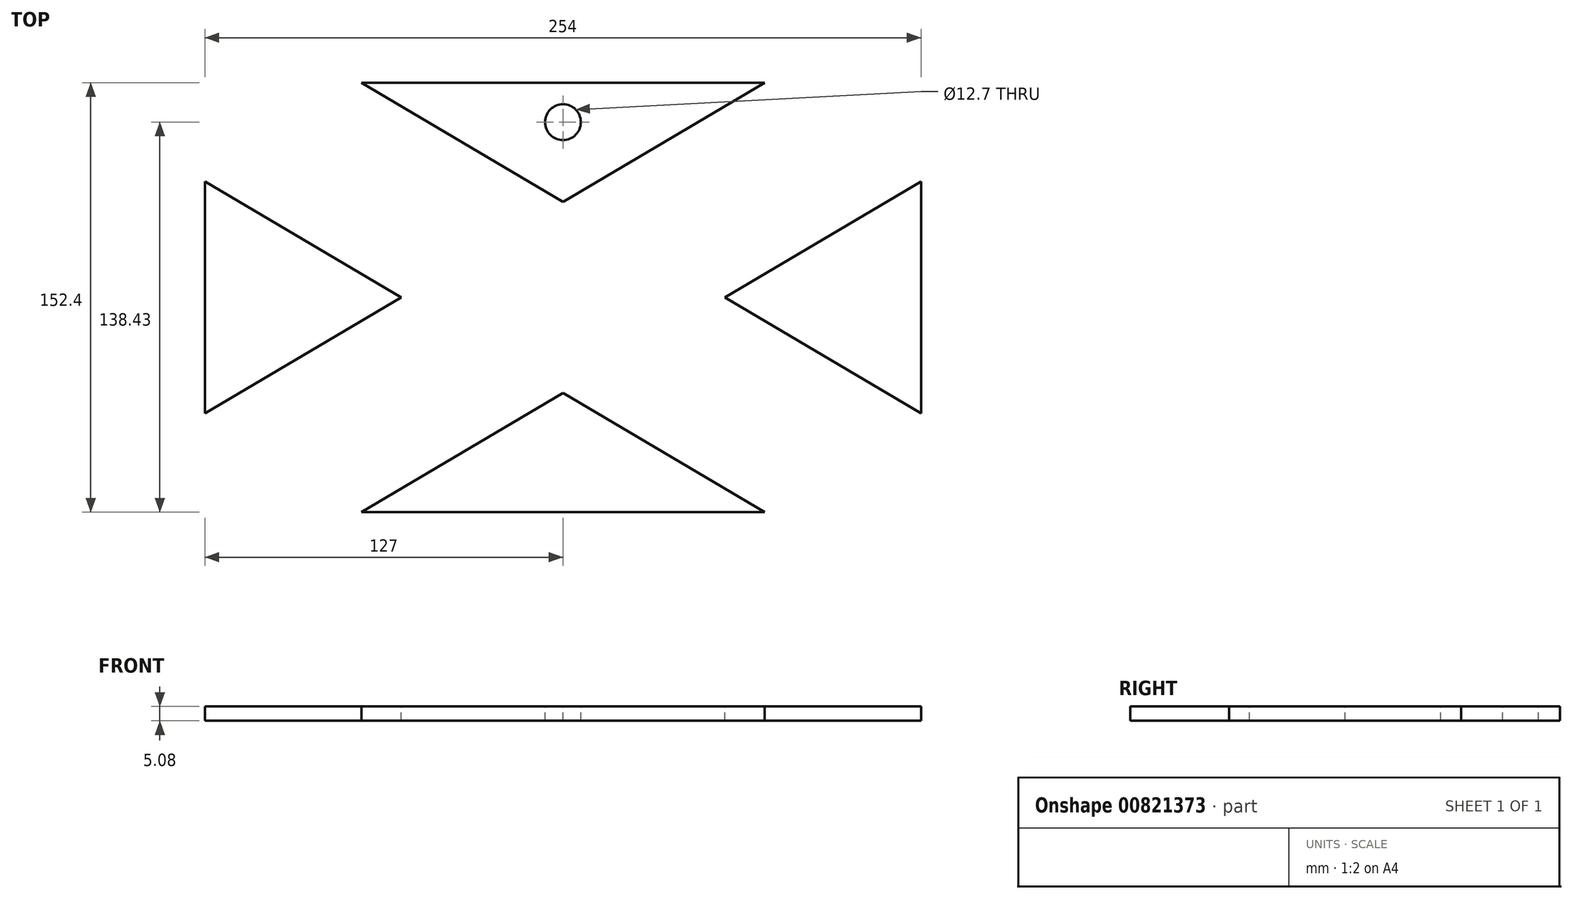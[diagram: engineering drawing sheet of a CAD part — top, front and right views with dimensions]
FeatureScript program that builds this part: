
annotation { "Feature Type Name" : "Feature", "Feature Type Description" : "" }
export const myFeature = defineFeature(function(context is Context, id is Id, definition is map)
    precondition{}
    {
        {
            var Q0;
            Q0=qCreatedBy(makeId("Top.planeOp"),FACE);
            var sketch = newSketch(context, id + "F0", { "sketchPlane" : qUnion([Q0])});
            skLineSegment(sketch, "E0.bottom", {"start": v(127, -76.2) * mm, "end": v(-127, -76.2) * mm});
            skLineSegment(sketch, "E0.top", {"start": v(127, 76.2) * mm, "end": v(-127, 76.2) * mm});
            skLineSegment(sketch, "E0.left", {"start": v(127, -76.2) * mm, "end": v(127, 76.2) * mm});
            skLineSegment(sketch, "E0.right", {"start": v(-127, -76.2) * mm, "end": v(-127, 76.2) * mm});
            skPoint(sketch, "E0.middle", {"position": v(0, 0) * mm});
            skSolve(sketch);
        }
        {
            var Q0;
            Q0=makeQuery(id+"F0.imprint","IMPRINT",FACE,{"disambiguationData":[TD([[makeQuery(id+"F0.imprint","IMPRINT",EDGE,{"derivedFrom":sQuery(id+"F0.wireOp",EDGE,"E0.bottom")}),-1.0]])]});
            var sketch = newSketch(context, id + "F1", { "sketchPlane" : qUnion([Q0])});
            skLineSegment(sketch, "E1.0", {"start": v(-127, -76.2) * mm, "end": v(-127, -55.88) * mm});
            skLineSegment(sketch, "E2.0", {"start": v(127, -76.2) * mm, "end": v(127, -55.88) * mm});
            skLineSegment(sketch, "E3.0", {"start": v(127, 76.2) * mm, "end": v(96.48, 76.2) * mm});
            skLineSegment(sketch, "E4.0", {"start": v(127, -76.2) * mm, "end": v(96.48, -76.2) * mm});
            skLineSegment(sketch, "E5", {"start": v(-127, -55.88) * mm, "end": v(96.48, 76.2) * mm});
            skLineSegment(sketch, "E6", {"start": v(-96.48, -76.2) * mm, "end": v(127, 55.88) * mm});
            skLineSegment(sketch, "E7", {"start": v(-127, 55.88) * mm, "end": v(96.48, -76.2) * mm});
            skLineSegment(sketch, "E8", {"start": v(127, -55.88) * mm, "end": v(-96.48, 76.2) * mm});
            skLineSegment(sketch, "E9.trimOffspring", {"start": v(-127, 55.88) * mm, "end": v(-127, 76.2) * mm});
            skLineSegment(sketch, "E10.trimOffspring", {"start": v(-96.48, 76.2) * mm, "end": v(-127, 76.2) * mm});
            skLineSegment(sketch, "E11.trimOffspring", {"start": v(127, 55.88) * mm, "end": v(127, 76.2) * mm});
            skLineSegment(sketch, "E12.trimOffspring", {"start": v(-96.48, -76.2) * mm, "end": v(-127, -76.2) * mm});
            skSolve(sketch);
        }
        {
            var Q0;
            Q0=makeQuery(id+"F0.imprint","IMPRINT",FACE,{"disambiguationData":[TD([[makeQuery(id+"F0.imprint","IMPRINT",EDGE,{"derivedFrom":sQuery(id+"F0.wireOp",EDGE,"E0.bottom")}),-1.0]])]});
            extrude(context, id + "F2", {"entities" : qUnion([Q0]), "depth" : 5.08 * mm, "offsetDistance" : 25.4 * mm});
        }
        {
            var Q0;
            Q0 = qSketchRegion(id + "F1", true);
            extrude(context, id + "F3", {"entities" : qUnion([Q0]), "depth" : 4.57 * mm, "offsetDistance" : 25.4 * mm});
        }
        {
            var Q0;
            Q0=makeQuery(id+"F3.opExtrude","CAP_FACE",FACE,{"disambiguationData":[OSD([sQuery(id+"F1.wireOp",EDGE,"E1.0"),sQuery(id+"F1.wireOp",EDGE,"E2.0"),sQuery(id+"F1.wireOp",EDGE,"E3.0"),sQuery(id+"F1.wireOp",EDGE,"E4.0"),sQuery(id+"F1.wireOp",EDGE,"E5"),sQuery(id+"F1.wireOp",EDGE,"E6"),sQuery(id+"F1.wireOp",EDGE,"E7"),sQuery(id+"F1.wireOp",EDGE,"E8"),sQuery(id+"F1.wireOp",EDGE,"E9.trimOffspring"),sQuery(id+"F1.wireOp",EDGE,"E10.trimOffspring"),sQuery(id+"F1.wireOp",EDGE,"E11.trimOffspring"),sQuery(id+"F1.wireOp",EDGE,"E12.trimOffspring")])],"isStart":false});
            var sketch = newSketch(context, id + "F4", { "sketchPlane" : qUnion([Q0])});
            skLineSegment(sketch, "E13", {"start": v(-47.84, 13) * mm, "end": v(-39.34, 19.17) * mm});
            skLineSegment(sketch, "E14", {"start": v(-25.6, 29.15) * mm, "end": v(-36.1, 29.15) * mm});
            skLineSegment(sketch, "E15", {"start": v(-53.09, 29.15) * mm, "end": v(-44.6, 22.98) * mm});
            skLineSegment(sketch, "E16", {"start": v(-30.85, 13) * mm, "end": v(-34.1, 22.98) * mm});
            skLineSegment(sketch, "E17", {"start": v(-39.34, 39.14) * mm, "end": v(-42.59, 29.15) * mm});
            skLineSegment(sketch, "E18", {"start": v(-79.1, 30.34) * mm, "end": v(-70.6, 36.5) * mm});
            skLineSegment(sketch, "E19", {"start": v(-56.85, 46.5) * mm, "end": v(-67.35, 46.5) * mm});
            skLineSegment(sketch, "E20", {"start": v(-84.34, 46.5) * mm, "end": v(-75.85, 40.32) * mm});
            skLineSegment(sketch, "E21", {"start": v(-62.1, 30.34) * mm, "end": v(-65.35, 40.32) * mm});
            skLineSegment(sketch, "E22", {"start": v(-70.6, 56.48) * mm, "end": v(-73.84, 46.5) * mm});
            skLineSegment(sketch, "E23", {"start": v(-110.4, 48.48) * mm, "end": v(-101.9, 54.65) * mm});
            skLineSegment(sketch, "E24", {"start": v(-88.16, 64.64) * mm, "end": v(-98.66, 64.64) * mm});
            skLineSegment(sketch, "E25", {"start": v(-115.65, 64.64) * mm, "end": v(-107.16, 58.46) * mm});
            skLineSegment(sketch, "E26", {"start": v(-93.41, 48.48) * mm, "end": v(-96.66, 58.46) * mm});
            skLineSegment(sketch, "E27", {"start": v(-101.9, 74.62) * mm, "end": v(-105.15, 64.64) * mm});
            skLineSegment(sketch, "E28.trimOffspring", {"start": v(-98.66, 64.64) * mm, "end": v(-101.9, 74.62) * mm});
            skLineSegment(sketch, "E29.trimOffspring", {"start": v(-105.15, 64.64) * mm, "end": v(-115.65, 64.64) * mm});
            skLineSegment(sketch, "E30.trimOffspring", {"start": v(-107.16, 58.46) * mm, "end": v(-110.4, 48.48) * mm});
            skLineSegment(sketch, "E31.trimOffspring", {"start": v(-101.9, 54.65) * mm, "end": v(-93.41, 48.48) * mm});
            skLineSegment(sketch, "E32.trimOffspring", {"start": v(-96.66, 58.46) * mm, "end": v(-88.16, 64.64) * mm});
            skLineSegment(sketch, "E33.trimOffspring", {"start": v(-75.85, 40.32) * mm, "end": v(-79.1, 30.34) * mm});
            skLineSegment(sketch, "E34.trimOffspring", {"start": v(-73.84, 46.5) * mm, "end": v(-84.34, 46.5) * mm});
            skLineSegment(sketch, "E35.trimOffspring", {"start": v(-67.35, 46.5) * mm, "end": v(-70.6, 56.48) * mm});
            skLineSegment(sketch, "E36.trimOffspring", {"start": v(-65.35, 40.32) * mm, "end": v(-56.85, 46.5) * mm});
            skLineSegment(sketch, "E37.trimOffspring", {"start": v(-70.6, 36.5) * mm, "end": v(-62.1, 30.34) * mm});
            skLineSegment(sketch, "E38.trimOffspring", {"start": v(-44.6, 22.98) * mm, "end": v(-47.84, 13) * mm});
            skLineSegment(sketch, "E39.trimOffspring", {"start": v(-42.59, 29.15) * mm, "end": v(-53.09, 29.15) * mm});
            skLineSegment(sketch, "E40.trimOffspring", {"start": v(-36.1, 29.15) * mm, "end": v(-39.34, 39.14) * mm});
            skLineSegment(sketch, "E41.trimOffspring", {"start": v(-34.1, 22.98) * mm, "end": v(-25.6, 29.15) * mm});
            skLineSegment(sketch, "E42.trimOffspring", {"start": v(-39.34, 19.17) * mm, "end": v(-30.85, 13) * mm});
            skLineSegment(sketch, "E43", {"start": v(92.71, 48.72) * mm, "end": v(101.2, 54.9) * mm});
            skLineSegment(sketch, "E44", {"start": v(114.95, 64.88) * mm, "end": v(104.45, 64.88) * mm});
            skLineSegment(sketch, "E45", {"start": v(87.46, 64.88) * mm, "end": v(95.96, 58.7) * mm});
            skLineSegment(sketch, "E46", {"start": v(109.7, 48.72) * mm, "end": v(106.46, 58.7) * mm});
            skLineSegment(sketch, "E47", {"start": v(101.2, 74.86) * mm, "end": v(97.96, 64.88) * mm});
            skLineSegment(sketch, "E48", {"start": v(60.3, 28.22) * mm, "end": v(68.8, 34.4) * mm});
            skLineSegment(sketch, "E49", {"start": v(82.54, 44.38) * mm, "end": v(72.04, 44.38) * mm});
            skLineSegment(sketch, "E50", {"start": v(55.05, 44.38) * mm, "end": v(63.54, 38.2) * mm});
            skLineSegment(sketch, "E51", {"start": v(77.29, 28.22) * mm, "end": v(74.04, 38.2) * mm});
            skLineSegment(sketch, "E52", {"start": v(68.8, 54.36) * mm, "end": v(65.55, 44.38) * mm});
            skLineSegment(sketch, "E53", {"start": v(26.46, 9.39) * mm, "end": v(34.95, 15.56) * mm});
            skLineSegment(sketch, "E54", {"start": v(48.7, 25.54) * mm, "end": v(38.2, 25.54) * mm});
            skLineSegment(sketch, "E55", {"start": v(21.2, 25.54) * mm, "end": v(29.7, 19.37) * mm});
            skLineSegment(sketch, "E56", {"start": v(43.45, 9.39) * mm, "end": v(40.2, 19.37) * mm});
            skLineSegment(sketch, "E57", {"start": v(34.95, 35.53) * mm, "end": v(31.7, 25.54) * mm});
            skLineSegment(sketch, "E58.trimOffspring", {"start": v(31.7, 25.54) * mm, "end": v(21.2, 25.54) * mm});
            skLineSegment(sketch, "E59.trimOffspring", {"start": v(29.7, 19.37) * mm, "end": v(26.46, 9.39) * mm});
            skLineSegment(sketch, "E60.trimOffspring", {"start": v(34.95, 15.56) * mm, "end": v(43.45, 9.39) * mm});
            skLineSegment(sketch, "E61.trimOffspring", {"start": v(40.2, 19.37) * mm, "end": v(48.7, 25.54) * mm});
            skLineSegment(sketch, "E62.trimOffspring", {"start": v(38.2, 25.54) * mm, "end": v(34.95, 35.53) * mm});
            skLineSegment(sketch, "E63.trimOffspring", {"start": v(63.54, 38.2) * mm, "end": v(60.3, 28.22) * mm});
            skLineSegment(sketch, "E64.trimOffspring", {"start": v(68.8, 34.4) * mm, "end": v(77.29, 28.22) * mm});
            skLineSegment(sketch, "E65.trimOffspring", {"start": v(74.04, 38.2) * mm, "end": v(82.54, 44.38) * mm});
            skLineSegment(sketch, "E66.trimOffspring", {"start": v(72.04, 44.38) * mm, "end": v(68.8, 54.36) * mm});
            skLineSegment(sketch, "E67.trimOffspring", {"start": v(65.55, 44.38) * mm, "end": v(55.05, 44.38) * mm});
            skLineSegment(sketch, "E68.trimOffspring", {"start": v(95.96, 58.7) * mm, "end": v(92.71, 48.72) * mm});
            skLineSegment(sketch, "E69.trimOffspring", {"start": v(106.46, 58.7) * mm, "end": v(114.95, 64.88) * mm});
            skLineSegment(sketch, "E70.trimOffspring", {"start": v(101.2, 54.9) * mm, "end": v(109.7, 48.72) * mm});
            skLineSegment(sketch, "E71.trimOffspring", {"start": v(97.96, 64.88) * mm, "end": v(87.46, 64.88) * mm});
            skLineSegment(sketch, "E72.trimOffspring", {"start": v(104.45, 64.88) * mm, "end": v(101.2, 74.86) * mm});
            skLineSegment(sketch, "E73", {"start": v(98.34, -73.56) * mm, "end": v(106.84, -67.39) * mm});
            skLineSegment(sketch, "E74", {"start": v(120.58, -57.4) * mm, "end": v(110.08, -57.4) * mm});
            skLineSegment(sketch, "E75", {"start": v(93.1, -57.4) * mm, "end": v(101.59, -63.57) * mm});
            skLineSegment(sketch, "E76", {"start": v(115.33, -73.56) * mm, "end": v(112.09, -63.57) * mm});
            skLineSegment(sketch, "E77", {"start": v(106.84, -47.41) * mm, "end": v(103.6, -57.4) * mm});
            skLineSegment(sketch, "E78", {"start": v(66.16, -55.85) * mm, "end": v(74.65, -49.67) * mm});
            skLineSegment(sketch, "E79", {"start": v(88.4, -39.69) * mm, "end": v(77.9, -39.69) * mm});
            skLineSegment(sketch, "E80", {"start": v(60.9, -39.69) * mm, "end": v(69.4, -45.86) * mm});
            skLineSegment(sketch, "E81", {"start": v(83.15, -55.85) * mm, "end": v(79.9, -45.86) * mm});
            skLineSegment(sketch, "E82", {"start": v(74.65, -29.7) * mm, "end": v(71.4, -39.69) * mm});
            skLineSegment(sketch, "E83", {"start": v(33.1, -36.4) * mm, "end": v(41.6, -30.23) * mm});
            skLineSegment(sketch, "E84", {"start": v(55.35, -20.25) * mm, "end": v(44.85, -20.25) * mm});
            skLineSegment(sketch, "E85", {"start": v(27.86, -20.25) * mm, "end": v(36.35, -26.42) * mm});
            skLineSegment(sketch, "E86", {"start": v(50.1, -36.4) * mm, "end": v(46.85, -26.42) * mm});
            skLineSegment(sketch, "E87", {"start": v(41.6, -10.26) * mm, "end": v(38.36, -20.25) * mm});
            skLineSegment(sketch, "E88.trimOffspring", {"start": v(44.85, -20.25) * mm, "end": v(41.6, -10.26) * mm});
            skLineSegment(sketch, "E89.trimOffspring", {"start": v(38.36, -20.25) * mm, "end": v(27.86, -20.25) * mm});
            skLineSegment(sketch, "E90.trimOffspring", {"start": v(36.35, -26.42) * mm, "end": v(33.1, -36.4) * mm});
            skLineSegment(sketch, "E91.trimOffspring", {"start": v(41.6, -30.23) * mm, "end": v(50.1, -36.4) * mm});
            skLineSegment(sketch, "E92.trimOffspring", {"start": v(46.85, -26.42) * mm, "end": v(55.35, -20.25) * mm});
            skLineSegment(sketch, "E93.trimOffspring", {"start": v(71.4, -39.69) * mm, "end": v(60.9, -39.69) * mm});
            skLineSegment(sketch, "E94.trimOffspring", {"start": v(69.4, -45.86) * mm, "end": v(66.16, -55.85) * mm});
            skLineSegment(sketch, "E95.trimOffspring", {"start": v(74.65, -49.67) * mm, "end": v(83.15, -55.85) * mm});
            skLineSegment(sketch, "E96.trimOffspring", {"start": v(79.9, -45.86) * mm, "end": v(88.4, -39.69) * mm});
            skLineSegment(sketch, "E97.trimOffspring", {"start": v(77.9, -39.69) * mm, "end": v(74.65, -29.7) * mm});
            skLineSegment(sketch, "E98.trimOffspring", {"start": v(103.6, -57.4) * mm, "end": v(93.1, -57.4) * mm});
            skLineSegment(sketch, "E99.trimOffspring", {"start": v(101.59, -63.57) * mm, "end": v(98.34, -73.56) * mm});
            skLineSegment(sketch, "E100.trimOffspring", {"start": v(106.84, -67.39) * mm, "end": v(115.33, -73.56) * mm});
            skLineSegment(sketch, "E101.trimOffspring", {"start": v(112.09, -63.57) * mm, "end": v(120.58, -57.4) * mm});
            skLineSegment(sketch, "E102.trimOffspring", {"start": v(110.08, -57.4) * mm, "end": v(106.84, -47.41) * mm});
            skLineSegment(sketch, "E103", {"start": v(-113.93, -72.57) * mm, "end": v(-105.44, -66.4) * mm});
            skLineSegment(sketch, "E104", {"start": v(-91.7, -56.41) * mm, "end": v(-102.2, -56.41) * mm});
            skLineSegment(sketch, "E105", {"start": v(-119.18, -56.41) * mm, "end": v(-110.69, -62.58) * mm});
            skLineSegment(sketch, "E106", {"start": v(-96.94, -72.57) * mm, "end": v(-100.19, -62.58) * mm});
            skLineSegment(sketch, "E107", {"start": v(-105.44, -46.43) * mm, "end": v(-108.68, -56.41) * mm});
            skLineSegment(sketch, "E108", {"start": v(-80.55, -53.31) * mm, "end": v(-72.06, -47.14) * mm});
            skLineSegment(sketch, "E109", {"start": v(-58.31, -37.15) * mm, "end": v(-68.81, -37.15) * mm});
            skLineSegment(sketch, "E110", {"start": v(-85.8, -37.15) * mm, "end": v(-77.3, -43.33) * mm});
            skLineSegment(sketch, "E111", {"start": v(-63.56, -53.31) * mm, "end": v(-66.8, -43.33) * mm});
            skLineSegment(sketch, "E112", {"start": v(-72.06, -27.17) * mm, "end": v(-75.3, -37.15) * mm});
            skLineSegment(sketch, "E113", {"start": v(-45.52, -32.65) * mm, "end": v(-37.02, -26.48) * mm});
            skLineSegment(sketch, "E114", {"start": v(-23.28, -16.5) * mm, "end": v(-33.78, -16.5) * mm});
            skLineSegment(sketch, "E115", {"start": v(-50.77, -16.5) * mm, "end": v(-42.27, -22.66) * mm});
            skLineSegment(sketch, "E116", {"start": v(-28.53, -32.65) * mm, "end": v(-31.77, -22.66) * mm});
            skLineSegment(sketch, "E117", {"start": v(-37.02, -6.5) * mm, "end": v(-40.27, -16.5) * mm});
            skLineSegment(sketch, "E118.trimOffspring", {"start": v(-40.27, -16.5) * mm, "end": v(-50.77, -16.5) * mm});
            skLineSegment(sketch, "E119.trimOffspring", {"start": v(-42.27, -22.66) * mm, "end": v(-45.52, -32.65) * mm});
            skLineSegment(sketch, "E120.trimOffspring", {"start": v(-37.02, -26.48) * mm, "end": v(-28.53, -32.65) * mm});
            skLineSegment(sketch, "E121.trimOffspring", {"start": v(-31.77, -22.66) * mm, "end": v(-23.28, -16.5) * mm});
            skLineSegment(sketch, "E122.trimOffspring", {"start": v(-33.78, -16.5) * mm, "end": v(-37.02, -6.5) * mm});
            skLineSegment(sketch, "E123.trimOffspring", {"start": v(-75.3, -37.15) * mm, "end": v(-85.8, -37.15) * mm});
            skLineSegment(sketch, "E124.trimOffspring", {"start": v(-77.3, -43.33) * mm, "end": v(-80.55, -53.31) * mm});
            skLineSegment(sketch, "E125.trimOffspring", {"start": v(-72.06, -47.14) * mm, "end": v(-63.56, -53.31) * mm});
            skLineSegment(sketch, "E126.trimOffspring", {"start": v(-66.8, -43.33) * mm, "end": v(-58.31, -37.15) * mm});
            skLineSegment(sketch, "E127.trimOffspring", {"start": v(-68.81, -37.15) * mm, "end": v(-72.06, -27.17) * mm});
            skLineSegment(sketch, "E128.trimOffspring", {"start": v(-108.68, -56.41) * mm, "end": v(-119.18, -56.41) * mm});
            skLineSegment(sketch, "E129.trimOffspring", {"start": v(-110.69, -62.58) * mm, "end": v(-113.93, -72.57) * mm});
            skLineSegment(sketch, "E130.trimOffspring", {"start": v(-105.44, -66.4) * mm, "end": v(-96.94, -72.57) * mm});
            skLineSegment(sketch, "E131.trimOffspring", {"start": v(-100.19, -62.58) * mm, "end": v(-91.7, -56.41) * mm});
            skLineSegment(sketch, "E132.trimOffspring", {"start": v(-102.2, -56.41) * mm, "end": v(-105.44, -46.43) * mm});
            skLineSegment(sketch, "E133", {"start": v(-8.5, -11.7) * mm, "end": v(0, -5.52) * mm});
            skLineSegment(sketch, "E134", {"start": v(13.74, 4.47) * mm, "end": v(3.24, 4.47) * mm});
            skLineSegment(sketch, "E135", {"start": v(-13.74, 4.47) * mm, "end": v(-5.25, -1.7) * mm});
            skLineSegment(sketch, "E136", {"start": v(8.5, -11.7) * mm, "end": v(5.25, -1.7) * mm});
            skLineSegment(sketch, "E137", {"start": v(0, 14.45) * mm, "end": v(-3.24, 4.47) * mm});
            skLineSegment(sketch, "E138.trimOffspring", {"start": v(3.24, 4.47) * mm, "end": v(0, 14.45) * mm});
            skLineSegment(sketch, "E139.trimOffspring", {"start": v(-3.24, 4.47) * mm, "end": v(-13.74, 4.47) * mm});
            skLineSegment(sketch, "E140.trimOffspring", {"start": v(-5.25, -1.7) * mm, "end": v(-8.5, -11.7) * mm});
            skLineSegment(sketch, "E141.trimOffspring", {"start": v(0, -5.52) * mm, "end": v(8.5, -11.7) * mm});
            skLineSegment(sketch, "E142.trimOffspring", {"start": v(5.25, -1.7) * mm, "end": v(13.74, 4.47) * mm});
            skSolve(sketch);
        }
        {
            var Q0;
            Q0 = qSketchRegion(id + "F4", true);
            extrude(context, id + "F5", {"entities" : qUnion([Q0]), "depth" : 0.5 * mm, "offsetDistance" : 25.4 * mm});
        }
        {
            var Q0;
            Q0=makeQuery(id+"F2.opExtrude","CAP_FACE",FACE,{"disambiguationData":[OSD([sQuery(id+"F0.wireOp",EDGE,"E0.bottom"),sQuery(id+"F0.wireOp",EDGE,"E0.top"),sQuery(id+"F0.wireOp",EDGE,"E0.left"),sQuery(id+"F0.wireOp",EDGE,"E0.right")])],"isStart":false});
            var sketch = newSketch(context, id + "F6", { "sketchPlane" : qUnion([Q0])});
            skCircle(sketch, "E143", {"center": v(0, 62.23) * mm, "radius": 6.35 * mm});
            skSolve(sketch);
        }
        {
            var Q0;
            Q0 = qSketchRegion(id + "F6", true);
            extrude(context, id + "F7", {"entities" : qUnion([Q0]), "operationType" : NewBodyOperationType.REMOVE, "oppositeDirection" : true, "depth" : 25.4 * mm, "offsetDistance" : 25.4 * mm});
        }
        {
            var Q0;
            {var subQ5=sQuery(id+"F1.wireOp",EDGE,"E1.0");Q0=makeQuery(id+"F1.imprint","IMPRINT",FACE,{"disambiguationData":[TD([[makeQuery(id+"F1.imprint","IMPRINT",EDGE,{"derivedFrom":subQ5}),-1.0]])]});}
            var Q1;
            {var subQ0=sQuery(id+"F1.wireOp",EDGE,"E7");var subQ1=sQuery(id+"F1.wireOp",EDGE,"E5");var subQ2=makeQuery(id+"F1.imprint","INTERSECT",VERTEX,{"derivedFrom":[subQ1,subQ0]});Q1=makeQuery(id+"F1.imprint","IMPRINT",FACE,{"disambiguationData":[TD([[makeQuery(id+"F1.imprint","IMPRINT",EDGE,{"disambiguationData":[TD([[subQ2,-1.0]])],"derivedFrom":subQ1}),-1.0]])]});}
            var Q2;
            {var subQ4=sQuery(id+"F1.wireOp",EDGE,"E2.0");Q2=makeQuery(id+"F1.imprint","IMPRINT",FACE,{"disambiguationData":[TD([[makeQuery(id+"F1.imprint","IMPRINT",EDGE,{"derivedFrom":subQ4}),1.0]])]});}
            var Q3;
            {var subQ6=sQuery(id+"F1.wireOp",EDGE,"E3.0");Q3=makeQuery(id+"F1.imprint","IMPRINT",FACE,{"disambiguationData":[TD([[makeQuery(id+"F1.imprint","IMPRINT",EDGE,{"derivedFrom":subQ6}),1.0]])]});}
            var Q4;
            {var subQ0=sQuery(id+"F1.wireOp",EDGE,"E9.trimOffspring");Q4=makeQuery(id+"F1.imprint","IMPRINT",FACE,{"disambiguationData":[TD([[makeQuery(id+"F1.imprint","IMPRINT",EDGE,{"derivedFrom":subQ0}),-1.0]])]});}
            extrude(context, id + "F8", {"entities" : qUnion([Q0, Q1, Q2, Q3, Q4]), "operationType" : NewBodyOperationType.REMOVE, "depth" : 25.4 * mm, "offsetDistance" : 25.4 * mm});
        }
        {
            var Q0;
            {var subQ0=sQuery(id+"F0.wireOp",EDGE,"E0.left");Q0=makeQuery(id+"F8.boolean.opBoolean","SPLIT",FACE,{"disambiguationData":[TD([makeQuery(id+"F2.opExtrude","SWEPT_FACE",FACE,{"disambiguationData":[OSD([subQ0])]})])],"derivedFrom":makeQuery(id+"F2.opExtrude","CAP_FACE",FACE,{"disambiguationData":[OSD([sQuery(id+"F0.wireOp",EDGE,"E0.bottom"),sQuery(id+"F0.wireOp",EDGE,"E0.top"),subQ0,sQuery(id+"F0.wireOp",EDGE,"E0.right")])],"isStart":false})});}
            var sketch = newSketch(context, id + "F9", { "sketchPlane" : qUnion([Q0])});
            skLineSegment(sketch, "E144.0", {"start": v(127, 55.88) * mm, "end": v(32.45, 0) * mm});
            skLineSegment(sketch, "E145.0", {"start": v(32.45, 0) * mm, "end": v(127, -55.88) * mm});
            skLineSegment(sketch, "E146.0", {"start": v(127, -55.88) * mm, "end": v(127, -41.13) * mm});
            skLineSegment(sketch, "E147", {"start": v(127, -41.13) * mm, "end": v(57.41, 0) * mm});
            skLineSegment(sketch, "E148", {"start": v(57.41, 0) * mm, "end": v(127, 41.13) * mm});
            skLineSegment(sketch, "E149.trimOffspring", {"start": v(127, 41.13) * mm, "end": v(127, 55.88) * mm});
            skSolve(sketch);
        }
        {
            var Q0;
            Q0 = qSketchRegion(id + "F9", true);
            extrude(context, id + "F10", {"entities" : qUnion([Q0]), "oppositeDirection" : true, "depth" : 5.08 * mm, "offsetDistance" : 25.4 * mm});
        }
        {
            var Q0;
            Q0=makeQuery(id+"F9.imprint","IMPRINT",FACE,{"disambiguationData":[TD([[makeQuery(id+"F9.imprint","IMPRINT",EDGE,{"derivedFrom":sQuery(id+"F9.wireOp",EDGE,"E144.0")}),1.0]])]});
            extrude(context, id + "F11", {"entities" : qUnion([Q0]), "operationType" : NewBodyOperationType.REMOVE, "oppositeDirection" : true, "depth" : 25.4 * mm, "offsetDistance" : 25.4 * mm});
        }
        {
            var Q0;
            {var subQ0=sQuery(id+"F0.wireOp",EDGE,"E0.bottom");Q0=makeQuery(id+"F8.boolean.opBoolean","SPLIT",FACE,{"disambiguationData":[TD([makeQuery(id+"F2.opExtrude","SWEPT_FACE",FACE,{"disambiguationData":[OSD([subQ0])]})])],"derivedFrom":makeQuery(id+"F2.opExtrude","CAP_FACE",FACE,{"disambiguationData":[OSD([subQ0,sQuery(id+"F0.wireOp",EDGE,"E0.top"),sQuery(id+"F0.wireOp",EDGE,"E0.left"),sQuery(id+"F0.wireOp",EDGE,"E0.right")])],"isStart":false})});}
            var sketch = newSketch(context, id + "F12", { "sketchPlane" : qUnion([Q0])});
            skLineSegment(sketch, "E150.0", {"start": v(96.48, -76.2) * mm, "end": v(0, -19.18) * mm});
            skLineSegment(sketch, "E151.0", {"start": v(0, -19.18) * mm, "end": v(-96.48, -76.2) * mm});
            skLineSegment(sketch, "E152.0", {"start": v(96.48, -76.2) * mm, "end": v(71.52, -76.2) * mm});
            skLineSegment(sketch, "E153", {"start": v(-71.52, -76.2) * mm, "end": v(0, -33.93) * mm});
            skLineSegment(sketch, "E154", {"start": v(0, -33.93) * mm, "end": v(71.52, -76.2) * mm});
            skLineSegment(sketch, "E155.trimOffspring", {"start": v(-71.52, -76.2) * mm, "end": v(-96.48, -76.2) * mm});
            skSolve(sketch);
        }
        {
            var Q0;
            Q0 = qSketchRegion(id + "F12", true);
            extrude(context, id + "F13", {"entities" : qUnion([Q0]), "oppositeDirection" : true, "depth" : 5.08 * mm, "offsetDistance" : 25.4 * mm});
        }
        {
            var Q0;
            Q0=makeQuery(id+"F12.imprint","IMPRINT",FACE,{"disambiguationData":[TD([[makeQuery(id+"F12.imprint","IMPRINT",EDGE,{"derivedFrom":sQuery(id+"F12.wireOp",EDGE,"E150.0")}),1.0]])]});
            extrude(context, id + "F14", {"entities" : qUnion([Q0]), "operationType" : NewBodyOperationType.REMOVE, "oppositeDirection" : true, "depth" : 25.4 * mm, "offsetDistance" : 25.4 * mm});
        }
        {
            var Q0;
            {var subQ0=sQuery(id+"F0.wireOp",EDGE,"E0.right");Q0=makeQuery(id+"F8.boolean.opBoolean","SPLIT",FACE,{"disambiguationData":[TD([makeQuery(id+"F2.opExtrude","SWEPT_FACE",FACE,{"disambiguationData":[OSD([subQ0])]})])],"derivedFrom":makeQuery(id+"F2.opExtrude","CAP_FACE",FACE,{"disambiguationData":[OSD([sQuery(id+"F0.wireOp",EDGE,"E0.bottom"),sQuery(id+"F0.wireOp",EDGE,"E0.top"),sQuery(id+"F0.wireOp",EDGE,"E0.left"),subQ0])],"isStart":false})});}
            var sketch = newSketch(context, id + "F15", { "sketchPlane" : qUnion([Q0])});
            skLineSegment(sketch, "E156.0", {"start": v(-32.45, 0) * mm, "end": v(-127, 55.88) * mm});
            skLineSegment(sketch, "E157.0", {"start": v(-32.45, 0) * mm, "end": v(-127, -55.88) * mm});
            skLineSegment(sketch, "E158.0", {"start": v(-127, -55.88) * mm, "end": v(-127, -41.13) * mm});
            skLineSegment(sketch, "E159", {"start": v(-127, 41.13) * mm, "end": v(-57.41, 0) * mm});
            skLineSegment(sketch, "E160", {"start": v(-57.41, 0) * mm, "end": v(-127, -41.13) * mm});
            skLineSegment(sketch, "E161.trimOffspring", {"start": v(-127, 41.13) * mm, "end": v(-127, 55.88) * mm});
            skSolve(sketch);
        }
        {
            var Q0;
            Q0 = qSketchRegion(id + "F15", true);
            extrude(context, id + "F16", {"entities" : qUnion([Q0]), "oppositeDirection" : true, "depth" : 5.08 * mm, "offsetDistance" : 25.4 * mm});
        }
        {
            var Q0;
            Q0=makeQuery(id+"F15.imprint","IMPRINT",FACE,{"disambiguationData":[TD([[makeQuery(id+"F15.imprint","IMPRINT",EDGE,{"derivedFrom":sQuery(id+"F15.wireOp",EDGE,"E156.0")}),1.0]])]});
            extrude(context, id + "F17", {"entities" : qUnion([Q0]), "operationType" : NewBodyOperationType.REMOVE, "oppositeDirection" : true, "depth" : 25.4 * mm, "offsetDistance" : 25.4 * mm});
        }
        {
            var Q0;
            {var subQ0=sQuery(id+"F0.wireOp",EDGE,"E0.top");Q0=makeQuery(id+"F8.boolean.opBoolean","SPLIT",FACE,{"disambiguationData":[TD([makeQuery(id+"F2.opExtrude","SWEPT_FACE",FACE,{"disambiguationData":[OSD([subQ0])]})])],"derivedFrom":makeQuery(id+"F2.opExtrude","CAP_FACE",FACE,{"disambiguationData":[OSD([sQuery(id+"F0.wireOp",EDGE,"E0.bottom"),subQ0,sQuery(id+"F0.wireOp",EDGE,"E0.left"),sQuery(id+"F0.wireOp",EDGE,"E0.right")])],"isStart":false})});}
            var sketch = newSketch(context, id + "F18", { "sketchPlane" : qUnion([Q0])});
            skLineSegment(sketch, "E162.0", {"start": v(96.48, 76.2) * mm, "end": v(71.52, 76.2) * mm});
            skLineSegment(sketch, "E163.0", {"start": v(-96.48, 76.2) * mm, "end": v(0, 19.18) * mm});
            skLineSegment(sketch, "E164.0", {"start": v(96.48, 76.2) * mm, "end": v(0, 19.18) * mm});
            skLineSegment(sketch, "E165", {"start": v(71.52, 76.2) * mm, "end": v(0, 33.93) * mm});
            skLineSegment(sketch, "E166", {"start": v(0, 33.93) * mm, "end": v(-71.52, 76.2) * mm});
            skLineSegment(sketch, "E167.trimOffspring", {"start": v(-71.52, 76.2) * mm, "end": v(-96.48, 76.2) * mm});
            skSolve(sketch);
        }
        {
            var Q0;
            Q0 = qSketchRegion(id + "F18", true);
            extrude(context, id + "F19", {"entities" : qUnion([Q0]), "oppositeDirection" : true, "depth" : 5.08 * mm, "offsetDistance" : 25.4 * mm});
        }
        {
            var Q0;
            Q0=makeQuery(id+"F18.imprint","IMPRINT",FACE,{"disambiguationData":[TD([[makeQuery(id+"F18.imprint","IMPRINT",EDGE,{"derivedFrom":sQuery(id+"F18.wireOp",EDGE,"E162.0")}),1.0]])]});
            extrude(context, id + "F20", {"entities" : qUnion([Q0]), "operationType" : NewBodyOperationType.REMOVE, "oppositeDirection" : true, "depth" : 25.4 * mm, "offsetDistance" : 25.4 * mm});
        }
    });
